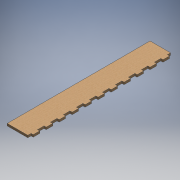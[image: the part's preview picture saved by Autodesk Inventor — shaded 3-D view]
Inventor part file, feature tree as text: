
AUTODESK INVENTOR PART (.ipt)
format: ipt  version: 2016 (Build 200138000, 138)  size: 178,176 bytes
history: native  units: mm
features: extrude x1, sketch x1
ambient origin geometry x8: Origin, YZ Plane, XZ Plane, XY Plane, X Axis, Y Axis, Z Axis, Center Point
bodies: Body1 (feature_tree)
feature tree (2):
  extrude  "Extrusion5"  Depth=6.39mm
  sketch  "Sketch2"  dims[d56=18.958829mm d58=6.39mm d70=110.0mm d72=37.917659mm d73=10.0mm d75=10.0mm d77=60.0mm d78=9.479415mm d79=9.479415mm d80=417.094246mm d94=6.39mm d95=0.0mm]
